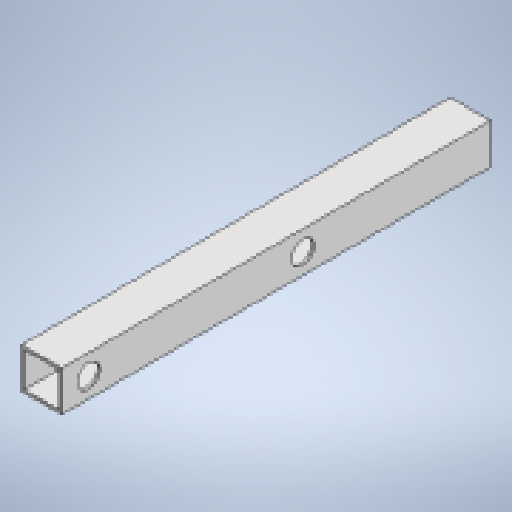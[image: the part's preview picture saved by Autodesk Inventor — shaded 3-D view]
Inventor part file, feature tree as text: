
AUTODESK INVENTOR PART (.ipt)
format: ipt  version: 2025.1 (Build 291241020, 241B)  size: 297,984 bytes
history: native  units: mm
features: extrude x2, sketch x2, projected_geometry x1
ambient origin geometry x8: Origin, YZ Plane, XZ Plane, XY Plane, X Axis, Y Axis, Z Axis, Center Point
bodies: Body1 (feature_tree)
feature tree (5):
  extrude  "Extrusion3"  Depth=30.0mm
  extrude  "Extrusion4"  Depth=2.0mm
  sketch  "Sketch9"  dims[d61=500.0mm d172=30.0mm]
  sketch  "Sketch10"  dims[d173=30.0mm d174=2.0mm d175=320.0mm d176=0.0mm d177=17.0mm d178=17.0mm d179=0.0mm d180=0.0mm d181=30.0mm d182=170.0mm d183=330.0mm d184=450.0mm d185=500.0mm d186=17.0mm]
  projected_geometry  "Projected Loop3"
